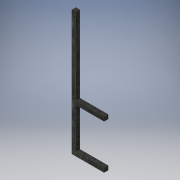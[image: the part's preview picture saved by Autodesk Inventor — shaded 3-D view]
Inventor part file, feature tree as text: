
AUTODESK INVENTOR PART (.ipt)
format: ipt  version: 2019 (Build 230136000, 136)  size: 111,616 bytes
history: native  units: mm
features: extrude x1, sketch x1
ambient origin geometry x8: Origin, YZ Plane, XZ Plane, XY Plane, X Axis, Y Axis, Z Axis, Center Point
bodies: Body1 (feature_tree)
feature tree (2):
  extrude  "Extrusion2"  Depth=10.0mm
  sketch  "Sketch2"  dims[d12=100.0mm d13=10.0mm d14=10.0mm d15=10.0mm d16=10.0mm d17=190.0mm d18=310.0mm d19=80.0mm d20=10.0mm d21=0.0mm]
